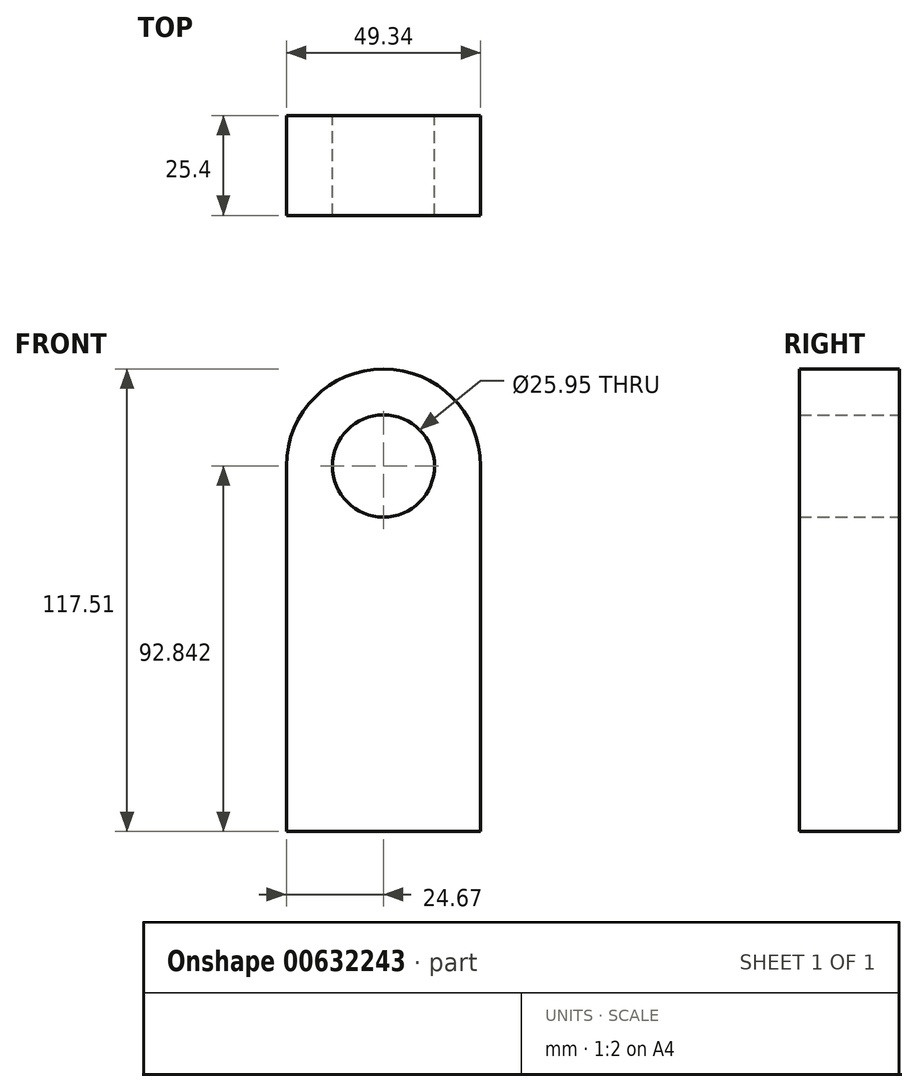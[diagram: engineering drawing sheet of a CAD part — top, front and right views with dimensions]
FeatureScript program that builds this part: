
annotation { "Feature Type Name" : "Feature", "Feature Type Description" : "" }
export const myFeature = defineFeature(function(context is Context, id is Id, definition is map)
    precondition{}
    {
        {
            var Q0;
            Q0=qCreatedBy(makeId("Front.planeOp"),FACE);
            var sketch = newSketch(context, id + "F0", { "sketchPlane" : qUnion([Q0])});
            skLineSegment(sketch, "E0.top", {"start": v(-24.67, -46.42) * mm, "end": v(24.67, -46.42) * mm});
            skLineSegment(sketch, "E0.left", {"start": v(-24.67, 46.42) * mm, "end": v(-24.67, -46.42) * mm});
            skLineSegment(sketch, "E0.right", {"start": v(24.67, 46.42) * mm, "end": v(24.67, -46.42) * mm});
            skPoint(sketch, "E0.middle", {"position": v(0, 0) * mm});
            skArc(sketch, "E1", {"start": v(24.67, 46.42) * mm, "mid": v(0, 71.1) * mm, "end": v(-24.67, 46.42) * mm});
            skCircle(sketch, "E2", {"center": v(0, 46.42) * mm, "radius": 12.98 * mm});
            skSolve(sketch);
        }
        {
            var Q0;
            Q0 = qSketchRegion(id + "F0", true);
            extrude(context, id + "F1", {"entities" : qUnion([Q0]), "depth" : 25.4 * mm, "offsetDistance" : 25.4 * mm});
        }
    });
